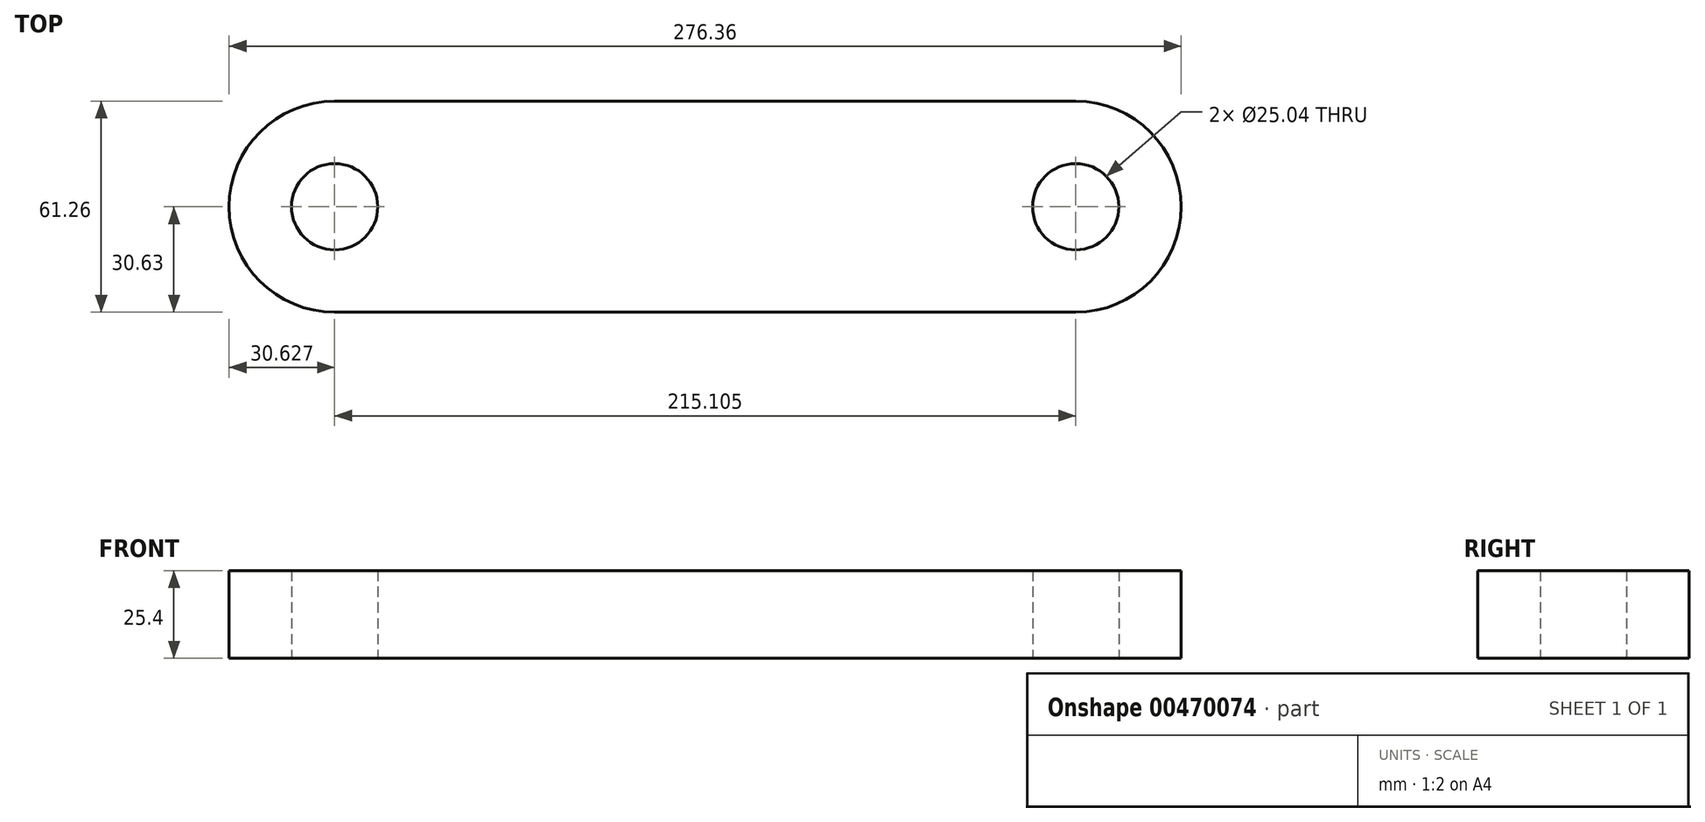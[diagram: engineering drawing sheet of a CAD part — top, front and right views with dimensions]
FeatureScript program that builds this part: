
annotation { "Feature Type Name" : "Feature", "Feature Type Description" : "" }
export const myFeature = defineFeature(function(context is Context, id is Id, definition is map)
    precondition{}
    {
        {
            var Q0;
            Q0=qCreatedBy(makeId("Top.planeOp"),FACE);
            var sketch = newSketch(context, id + "F0", { "sketchPlane" : qUnion([Q0])});
            skLineSegment(sketch, "E0.bottom", {"start": v(-107.55, 30.63) * mm, "end": v(107.55, 30.63) * mm});
            skLineSegment(sketch, "E0.top", {"start": v(-107.55, -30.63) * mm, "end": v(107.55, -30.63) * mm});
            skPoint(sketch, "E0.middle", {"position": v(0, 0) * mm});
            skArc(sketch, "E1", {"start": v(-107.55, 30.63) * mm, "mid": v(-138.18, 0) * mm, "end": v(-107.55, -30.63) * mm});
            skArc(sketch, "E2", {"start": v(107.55, -30.63) * mm, "mid": v(138.18, 0) * mm, "end": v(107.55, 30.63) * mm});
            skCircle(sketch, "E3", {"center": v(-107.55, 0) * mm, "radius": 12.52 * mm});
            skCircle(sketch, "E4", {"center": v(107.55, 0) * mm, "radius": 12.52 * mm});
            skSolve(sketch);
        }
        {
            var Q0;
            Q0=makeQuery(id+"F0.imprint","IMPRINT",FACE,{"disambiguationData":[TD([[makeQuery(id+"F0.imprint","IMPRINT",EDGE,{"derivedFrom":sQuery(id+"F0.wireOp",EDGE,"E0.bottom")}),-1.0]])]});
            extrude(context, id + "F1", {"entities" : qUnion([Q0]), "depth" : 25.4 * mm});
        }
    });
